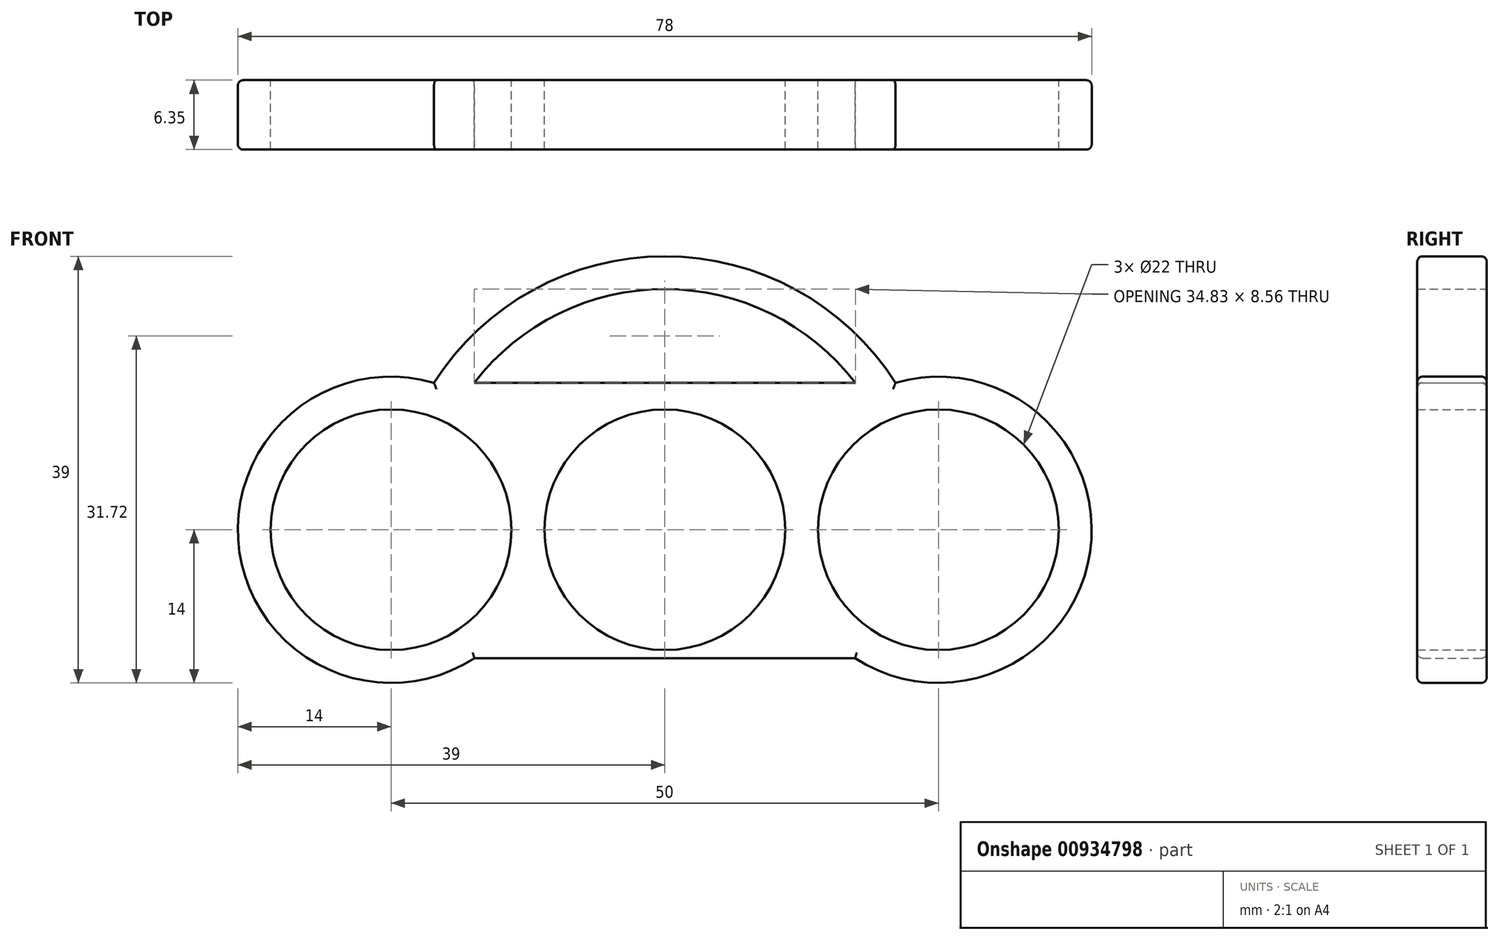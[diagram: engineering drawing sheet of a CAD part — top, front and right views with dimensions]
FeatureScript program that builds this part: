
annotation { "Feature Type Name" : "Feature", "Feature Type Description" : "" }
export const myFeature = defineFeature(function(context is Context, id is Id, definition is map)
    precondition{}
    {
        {
            var Q0;
            Q0=qCreatedBy(makeId("Front.planeOp"),FACE);
            var sketch = newSketch(context, id + "F0", { "sketchPlane" : qUnion([Q0])});
            skCircle(sketch, "E0", {"center": v(0, 0) * mm, "radius": 11 * mm});
            skCircle(sketch, "E1", {"center": v(-25, 0) * mm, "radius": 11 * mm});
            skCircle(sketch, "E2", {"center": v(25, 0) * mm, "radius": 11 * mm});
            skArc(sketch, "E3", {"start": v(-21.08, 13.44) * mm, "mid": v(-38.85, -2.03) * mm, "end": v(-17.39, -11.75) * mm});
            skArc(sketch, "E4", {"start": v(17.39, -11.75) * mm, "mid": v(38.85, -2.03) * mm, "end": v(21.08, 13.44) * mm});
            skArc(sketch, "E5.trimOffspring", {"start": v(21.08, 13.44) * mm, "mid": v(0, 25) * mm, "end": v(-21.08, 13.44) * mm});
            skArc(sketch, "E6", {"start": v(17.42, 13.44) * mm, "mid": v(10.37, 19.4) * mm, "end": v(1.5, 21.95) * mm});
            skLineSegment(sketch, "E7", {"start": v(-17.42, 13.44) * mm, "end": v(1.5, 13.44) * mm});
            skLineSegment(sketch, "E8.trimOffspring", {"start": v(1.5, 13.44) * mm, "end": v(17.42, 13.44) * mm});
            skArc(sketch, "E9.trimOffspring", {"start": v(1.5, 21.95) * mm, "mid": v(-9.02, 20.06) * mm, "end": v(-17.42, 13.44) * mm});
            skLineSegment(sketch, "E10", {"start": v(-17.39, -11.75) * mm, "end": v(17.39, -11.75) * mm});
            skPoint(sketch, "E11.start.orphan", {"position": v(0, -11) * mm});
            skSolve(sketch);
        }
        {
            var Q0;
            Q0=makeQuery(id+"F0.imprint","IMPRINT",FACE,{"disambiguationData":[TD([[makeQuery(id+"F0.imprint","IMPRINT",EDGE,{"derivedFrom":sQuery(id+"F0.wireOp",EDGE,"E0")}),-1.0]])]});
            extrude(context, id + "F1", {"entities" : qUnion([Q0]), "depth" : 6.35 * mm, "offsetDistance" : 25 * mm});
        }
        {
            var Q0;
            Q0=makeQuery(id+"F1.opExtrude","CAP_EDGE",EDGE,{"disambiguationData":[OSD([sQuery(id+"F0.wireOp",EDGE,"E3")])],"isStart":false});
            var Q1;
            Q1=makeQuery(id+"F1.opExtrude","CAP_EDGE",EDGE,{"disambiguationData":[OSD([sQuery(id+"F0.wireOp",EDGE,"E5.trimOffspring")])],"isStart":false});
            var Q2;
            Q2=makeQuery(id+"F1.opExtrude","CAP_EDGE",EDGE,{"disambiguationData":[OSD([sQuery(id+"F0.wireOp",EDGE,"E4")])],"isStart":false});
            var Q3;
            Q3=makeQuery(id+"F1.opExtrude","CAP_EDGE",EDGE,{"disambiguationData":[OSD([sQuery(id+"F0.wireOp",EDGE,"E10")])],"isStart":false});
            var Q4;
            Q4=makeQuery(id+"F1.opExtrude","CAP_EDGE",EDGE,{"disambiguationData":[OSD([sQuery(id+"F0.wireOp",EDGE,"E4")])],"isStart":true});
            var Q5;
            Q5=makeQuery(id+"F1.opExtrude","CAP_EDGE",EDGE,{"disambiguationData":[OSD([sQuery(id+"F0.wireOp",EDGE,"E5.trimOffspring")])],"isStart":true});
            var Q6;
            Q6=makeQuery(id+"F1.opExtrude","CAP_EDGE",EDGE,{"disambiguationData":[OSD([sQuery(id+"F0.wireOp",EDGE,"E3")])],"isStart":true});
            var Q7;
            Q7=makeQuery(id+"F1.opExtrude","CAP_EDGE",EDGE,{"disambiguationData":[OSD([sQuery(id+"F0.wireOp",EDGE,"E10")])],"isStart":true});
            fillet(context, id + "F2", {"entities" : qUnion([Q0, Q1, Q2, Q3, Q4, Q5, Q6, Q7]), "radius" : .5 * mm, "tangentPropagation" : true, "allowEdgeOverflow" : false});
        }
    });
